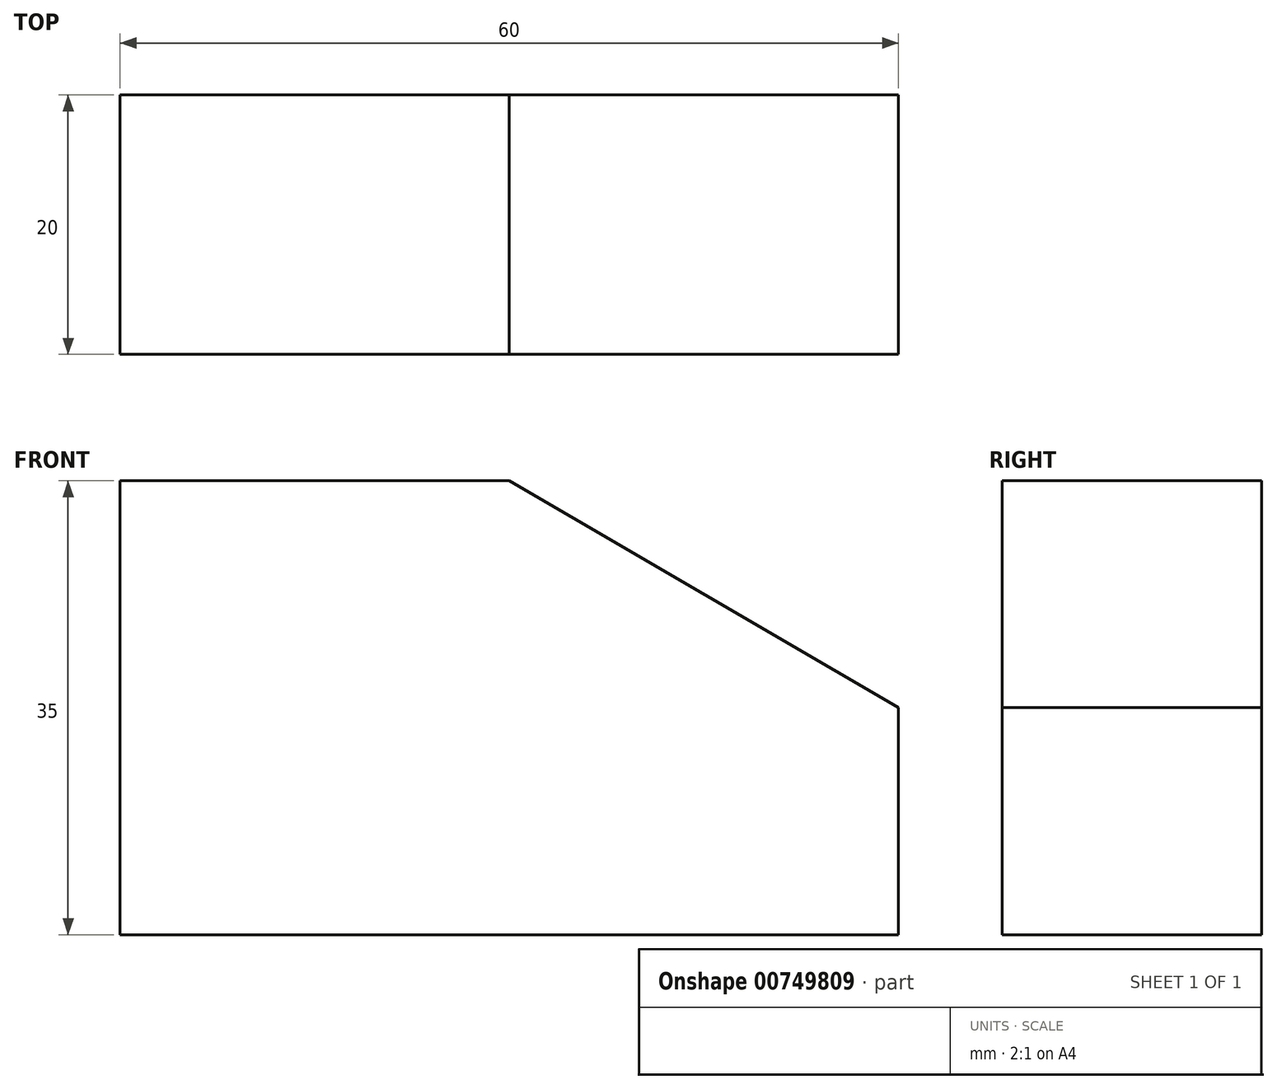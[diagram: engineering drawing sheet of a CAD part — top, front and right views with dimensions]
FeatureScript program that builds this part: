
annotation { "Feature Type Name" : "Feature", "Feature Type Description" : "" }
export const myFeature = defineFeature(function(context is Context, id is Id, definition is map)
    precondition{}
    {
        {
            var Q0;
            Q0=qCreatedBy(makeId("Top.planeOp"),FACE);
            var sketch = newSketch(context, id + "F0", { "sketchPlane" : qUnion([Q0])});
            skLineSegment(sketch, "E0.bottom", {"start": v(0, 0) * mm, "end": v(60, 0) * mm});
            skLineSegment(sketch, "E0.top", {"start": v(0, 20) * mm, "end": v(60, 20) * mm});
            skLineSegment(sketch, "E0.left", {"start": v(0, 0) * mm, "end": v(0, 20) * mm});
            skLineSegment(sketch, "E0.right", {"start": v(60, 0) * mm, "end": v(60, 20) * mm});
            skSolve(sketch);
        }
        {
            var Q0;
            Q0 = qSketchRegion(id + "F0", true);
            var Q1;
            Q1=makeQuery(id+"F0.imprint","IMPRINT",FACE,{"disambiguationData":[TD([[makeQuery(id+"F0.imprint","IMPRINT",EDGE,{"derivedFrom":sQuery(id+"F0.wireOp",EDGE,"E0.bottom")}),1.0]])]});
            extrude(context, id + "F1", {"entities" : qUnion([Q0, Q1]), "depth" : 35 * mm, "offsetDistance" : 25 * mm});
        }
        {
            var Q0;
            Q0=makeQuery(id+"F1.opExtrude","CAP_EDGE",EDGE,{"disambiguationData":[OSD([sQuery(id+"F0.wireOp",EDGE,"E0.right")])],"isStart":false});
            chamfer(context, id + "F2", {"entities" : qUnion([Q0]), "chamferType" : ChamferType.TWO_OFFSETS, "width1" : 30 * mm, "oppositeDirection" : false, "width2" : 17.5 * mm, "tangentPropagation" : true});
        }
    });
